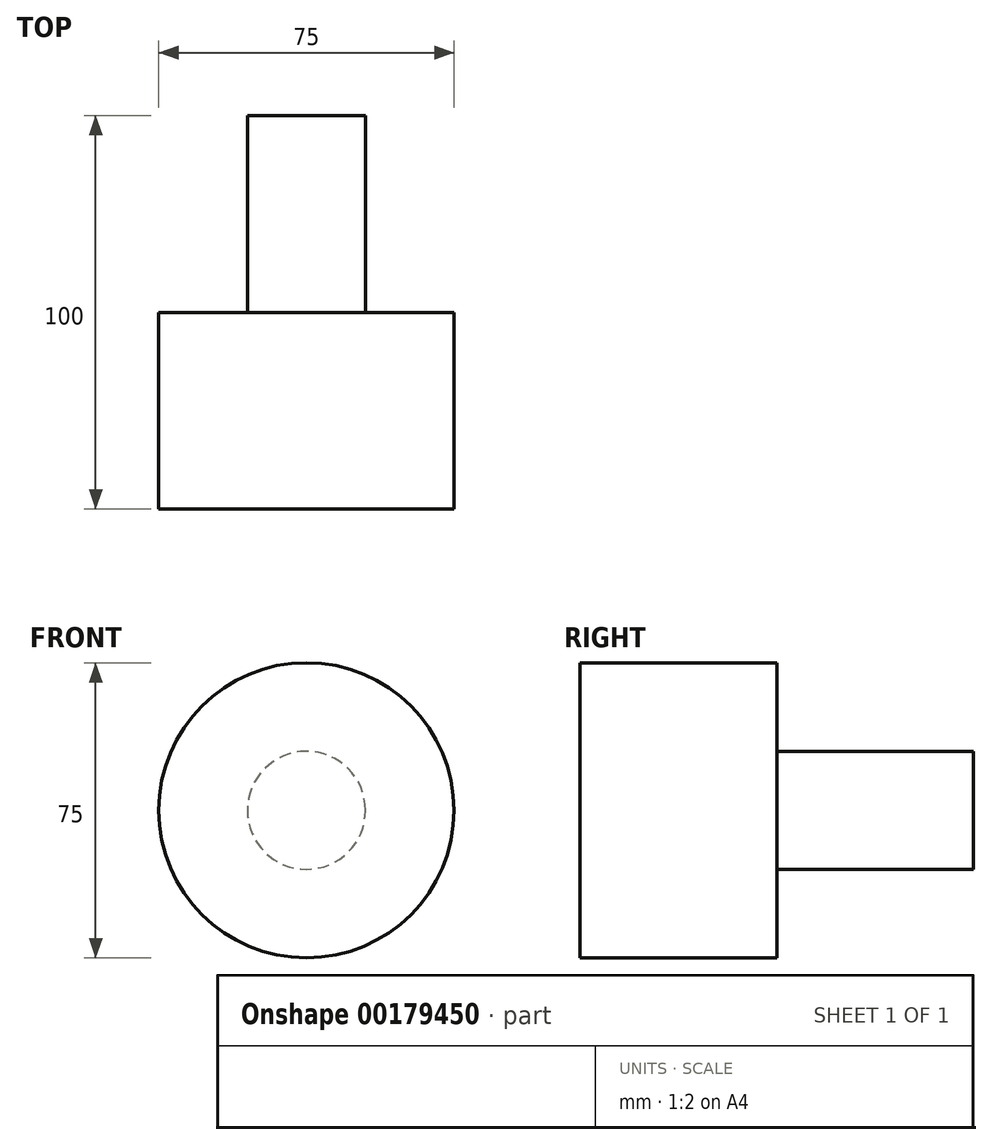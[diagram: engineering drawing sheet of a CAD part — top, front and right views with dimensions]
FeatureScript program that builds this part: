
annotation { "Feature Type Name" : "Feature", "Feature Type Description" : "" }
export const myFeature = defineFeature(function(context is Context, id is Id, definition is map)
    precondition{}
    {
        {
            var Q0;
            Q0=qCreatedBy(makeId("Front.planeOp"),FACE);
            var sketch = newSketch(context, id + "F0", { "sketchPlane" : qUnion([Q0])});
            skCircle(sketch, "E0", {"center": v(0, 0) * mm, "radius": 37.5 * mm});
            skCircle(sketch, "E1", {"center": v(0, 0) * mm, "radius": 15 * mm});
            skSolve(sketch);
        }
        {
            var Q0;
            Q0=makeQuery(id+"F0.imprint","IMPRINT",FACE,{"disambiguationData":[TD([[makeQuery(id+"F0.imprint","IMPRINT",EDGE,{"derivedFrom":sQuery(id+"F0.wireOp",EDGE,"E1")}),1.0]])]});
            extrude(context, id + "F1", {"entities" : qUnion([Q0]), "oppositeDirection" : true, "depth" : 100 * mm});
        }
        {
            var Q0;
            Q0=makeQuery(id+"F0.imprint","IMPRINT",FACE,{"disambiguationData":[TD([[makeQuery(id+"F0.imprint","IMPRINT",EDGE,{"derivedFrom":sQuery(id+"F0.wireOp",EDGE,"E0")}),1.0]])]});
            extrude(context, id + "F2", {"entities" : qUnion([Q0]), "operationType" : NewBodyOperationType.ADD, "oppositeDirection" : true, "depth" : 50 * mm});
        }
    });
